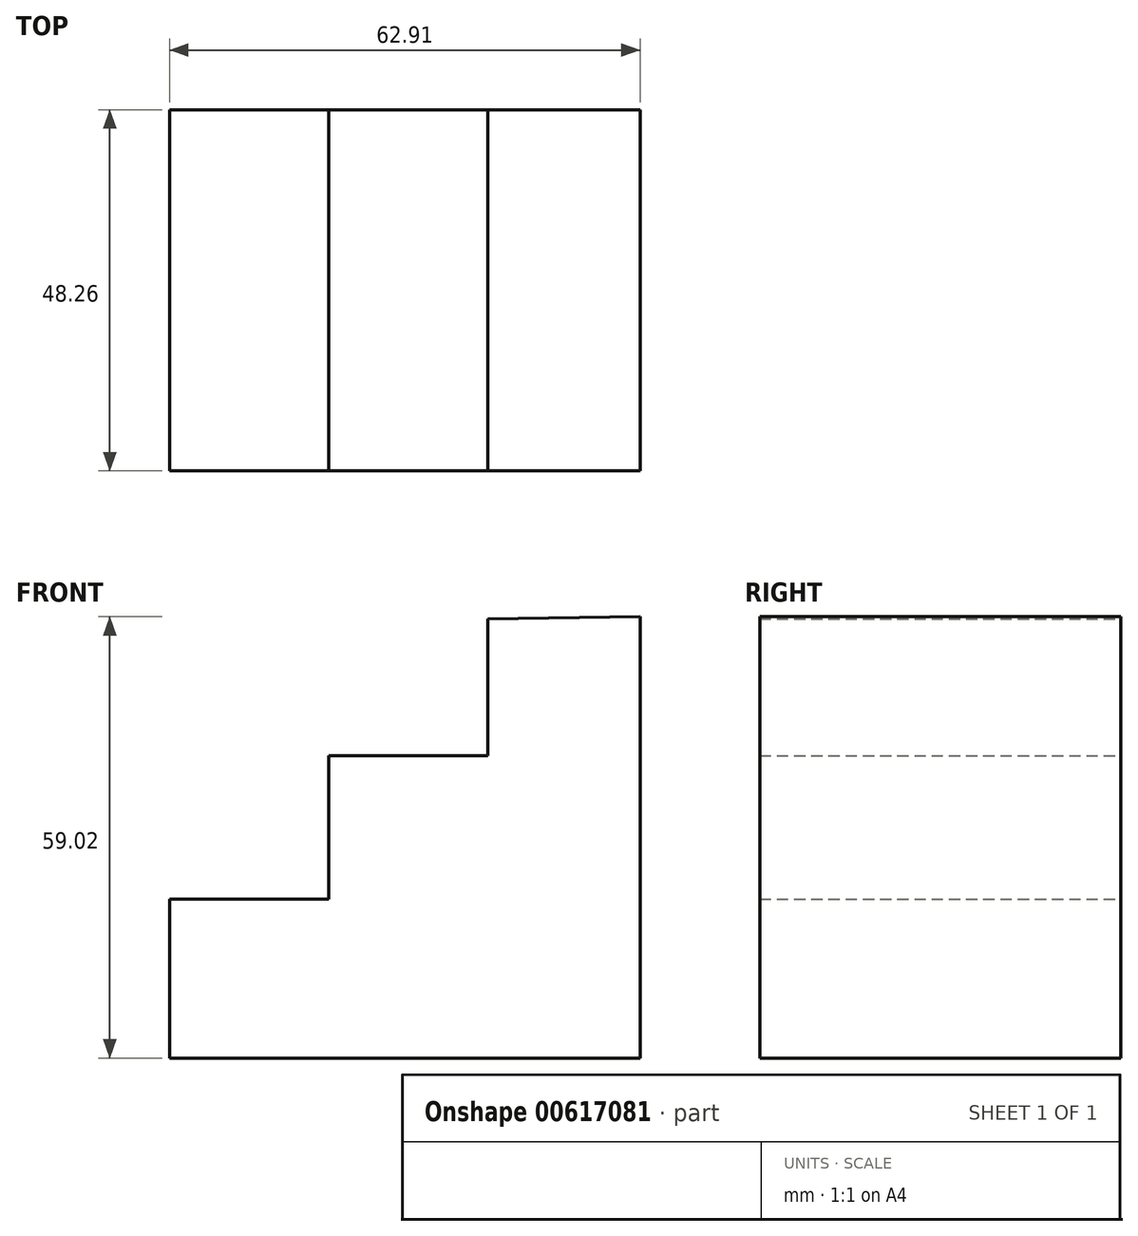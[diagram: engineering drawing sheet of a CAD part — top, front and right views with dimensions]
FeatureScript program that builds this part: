
annotation { "Feature Type Name" : "Feature", "Feature Type Description" : "" }
export const myFeature = defineFeature(function(context is Context, id is Id, definition is map)
    precondition{}
    {
        {
            var Q0;
            Q0=qCreatedBy(makeId("Front.planeOp"),FACE);
            var sketch = newSketch(context, id + "F0", { "sketchPlane" : qUnion([Q0])});
            skLineSegment(sketch, "E0", {"start": v(41.64, 31.27) * mm, "end": v(41.64, -27.75) * mm});
            skLineSegment(sketch, "E1", {"start": v(41.64, -27.75) * mm, "end": v(-21.27, -27.75) * mm});
            skLineSegment(sketch, "E2", {"start": v(-21.27, -27.75) * mm, "end": v(-21.27, -6.48) * mm});
            skLineSegment(sketch, "E3", {"start": v(-21.27, -6.48) * mm, "end": v(0, -6.48) * mm});
            skLineSegment(sketch, "E4", {"start": v(0, -6.48) * mm, "end": v(0, 12.7) * mm});
            skLineSegment(sketch, "E5", {"start": v(0, 12.7) * mm, "end": v(21.27, 12.7) * mm});
            skLineSegment(sketch, "E6", {"start": v(21.27, 12.7) * mm, "end": v(21.27, 30.97) * mm});
            skLineSegment(sketch, "E7", {"start": v(21.27, 30.97) * mm, "end": v(41.64, 31.27) * mm});
            skSolve(sketch);
        }
        {
            var Q0;
            Q0 = qSketchRegion(id + "F0", true);
            extrude(context, id + "F1", {"entities" : qUnion([Q0]), "depth" : 48.26 * mm, "offsetDistance" : 25.4 * mm});
        }
    });
